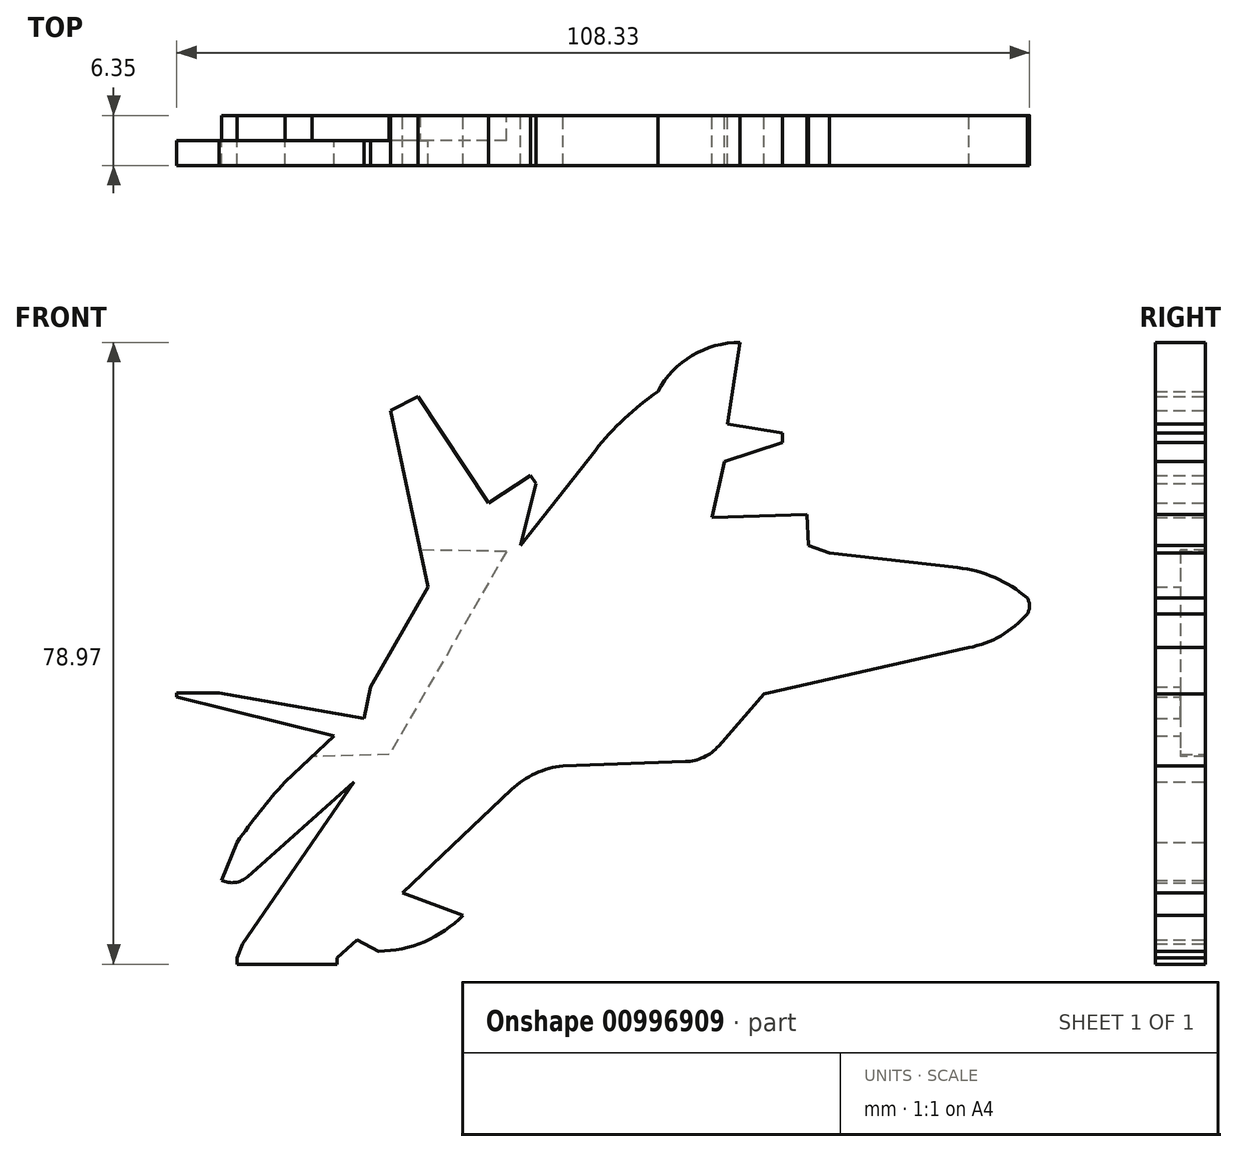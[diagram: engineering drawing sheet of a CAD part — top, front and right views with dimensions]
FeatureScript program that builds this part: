
annotation { "Feature Type Name" : "Feature", "Feature Type Description" : "" }
export const myFeature = defineFeature(function(context is Context, id is Id, definition is map)
    precondition{}
    {
        {
            var Q0;
            Q0=qCreatedBy(makeId("Front.planeOp"),FACE);
            var sketch = newSketch(context, id + "F0", { "sketchPlane" : qUnion([Q0])});
            skLineSegment(sketch, "E0", {"start": v(-31.83, -6.62) * mm, "end": v(-24.5, 6.08) * mm});
            skLineSegment(sketch, "E1", {"start": v(-24.5, 6.08) * mm, "end": v(-29.32, 28.52) * mm});
            skLineSegment(sketch, "E2", {"start": v(-29.32, 28.52) * mm, "end": v(-25.77, 30.29) * mm});
            skLineSegment(sketch, "E3", {"start": v(-25.77, 30.29) * mm, "end": v(-16.87, 16.76) * mm});
            skLineSegment(sketch, "E4", {"start": v(-16.87, 16.76) * mm, "end": v(-11.52, 20.28) * mm});
            skLineSegment(sketch, "E5", {"start": v(-11.52, 20.28) * mm, "end": v(-10.82, 19.22) * mm});
            skLineSegment(sketch, "E6", {"start": v(-10.82, 19.22) * mm, "end": v(-12.8, 11.37) * mm});
            skLineSegment(sketch, "E7", {"start": v(-12.8, 11.37) * mm, "end": v(-3.28, 23.46) * mm});
            skArc(sketch, "E8", {"start": v(4.67, 30.93) * mm, "mid": v(0.41, 27.5) * mm, "end": v(-3.28, 23.46) * mm});
            skArc(sketch, "E9", {"start": v(15.12, 37.16) * mm, "mid": v(9.03, 35.5) * mm, "end": v(4.67, 30.93) * mm});
            skLineSegment(sketch, "E10", {"start": v(15.12, 37.16) * mm, "end": v(13.48, 26.79) * mm});
            skLineSegment(sketch, "E11", {"start": v(13.48, 26.79) * mm, "end": v(20.5, 25.68) * mm});
            skLineSegment(sketch, "E12", {"start": v(20.5, 25.68) * mm, "end": v(20.5, 24.48) * mm});
            skLineSegment(sketch, "E13", {"start": v(20.5, 24.48) * mm, "end": v(13.12, 22.05) * mm});
            skLineSegment(sketch, "E14", {"start": v(13.12, 22.05) * mm, "end": v(11.53, 14.9) * mm});
            skLineSegment(sketch, "E15", {"start": v(11.53, 14.9) * mm, "end": v(23.64, 15.31) * mm});
            skLineSegment(sketch, "E16", {"start": v(23.64, 15.31) * mm, "end": v(23.77, 11.4) * mm});
            skLineSegment(sketch, "E17", {"start": v(23.77, 11.4) * mm, "end": v(26.46, 10.4) * mm});
            skLineSegment(sketch, "E18", {"start": v(26.46, 10.4) * mm, "end": v(42.75, 8.56) * mm});
            skArc(sketch, "E19", {"start": v(51.59, 4.7) * mm, "mid": v(47.46, 7.3) * mm, "end": v(42.75, 8.56) * mm});
            skArc(sketch, "E20", {"start": v(51.59, 2.7) * mm, "mid": v(51.88, 3.7) * mm, "end": v(51.59, 4.7) * mm});
            skArc(sketch, "E21", {"start": v(44.15, -1.6) * mm, "mid": v(48.24, -0.1) * mm, "end": v(51.59, 2.7) * mm});
            skLineSegment(sketch, "E22", {"start": v(44.15, -1.6) * mm, "end": v(18.14, -7.5) * mm});
            skLineSegment(sketch, "E23", {"start": v(18.14, -7.5) * mm, "end": v(12.4, -14.08) * mm});
            skArc(sketch, "E24", {"start": v(8.16, -16.1) * mm, "mid": v(10.49, -15.53) * mm, "end": v(12.4, -14.08) * mm});
            skLineSegment(sketch, "E25", {"start": v(8.16, -16.1) * mm, "end": v(-7.38, -16.6) * mm});
            skArc(sketch, "E26", {"start": v(-7.38, -16.6) * mm, "mid": v(-10.88, -17.59) * mm, "end": v(-13.9, -19.63) * mm});
            skLineSegment(sketch, "E27", {"start": v(-13.9, -19.63) * mm, "end": v(-27.78, -32.74) * mm});
            skLineSegment(sketch, "E28", {"start": v(-27.78, -32.74) * mm, "end": v(-20.07, -35.6) * mm});
            skArc(sketch, "E29", {"start": v(-30.81, -40.18) * mm, "mid": v(-24.99, -38.96) * mm, "end": v(-20.07, -35.6) * mm});
            skLineSegment(sketch, "E30", {"start": v(-30.81, -40.18) * mm, "end": v(-33.58, -38.72) * mm});
            skLineSegment(sketch, "E31", {"start": v(-33.58, -38.72) * mm, "end": v(-46.76, -50.69) * mm});
            skArc(sketch, "E32", {"start": v(-49.29, -51.48) * mm, "mid": v(-47.94, -51.36) * mm, "end": v(-46.76, -50.69) * mm});
            skLineSegment(sketch, "E33", {"start": v(-49.29, -51.48) * mm, "end": v(-52.27, -49.73) * mm});
            skLineSegment(sketch, "E34", {"start": v(-52.27, -49.73) * mm, "end": v(-48.1, -39.25) * mm});
            skLineSegment(sketch, "E35", {"start": v(-48.1, -39.25) * mm, "end": v(-33.9, -18.7) * mm});
            skLineSegment(sketch, "E36", {"start": v(-33.9, -18.7) * mm, "end": v(-47.44, -30.71) * mm});
            skArc(sketch, "E37", {"start": v(-50.76, -31.15) * mm, "mid": v(-49.03, -31.44) * mm, "end": v(-47.44, -30.71) * mm});
            skLineSegment(sketch, "E38", {"start": v(-50.76, -31.15) * mm, "end": v(-48.78, -26.37) * mm});
            skArc(sketch, "E39", {"start": v(-42.7, -18.7) * mm, "mid": v(-45.89, -22.42) * mm, "end": v(-48.78, -26.37) * mm});
            skLineSegment(sketch, "E40", {"start": v(-42.7, -18.7) * mm, "end": v(-36.44, -12.83) * mm});
            skLineSegment(sketch, "E41", {"start": v(-36.44, -12.83) * mm, "end": v(-56.45, -7.89) * mm});
            skLineSegment(sketch, "E42", {"start": v(-56.45, -7.89) * mm, "end": v(-56.45, -7.36) * mm});
            skLineSegment(sketch, "E43", {"start": v(-56.45, -7.36) * mm, "end": v(-51.06, -7.36) * mm});
            skLineSegment(sketch, "E44", {"start": v(-51.06, -7.36) * mm, "end": v(-32.68, -10.58) * mm});
            skLineSegment(sketch, "E45", {"start": v(-32.68, -10.58) * mm, "end": v(-31.83, -6.62) * mm});
            skLineSegment(sketch, "E46", {"start": v(-31.83, -6.62) * mm, "end": v(0, -6.62) * mm, "construction": true});
            skSolve(sketch);
        }
        {
            var Q0;
            Q0 = qSketchRegion(id + "F0", true);
            extrude(context, id + "F1", {"entities" : qUnion([Q0]), "depth" : 6.35 * mm, "offsetDistance" : 25.4 * mm});
        }
        {
            var Q0;
            Q0=makeQuery(id+"F1.opExtrude","CAP_FACE",FACE,{"disambiguationData":[OSD([sQuery(id+"F0.wireOp",EDGE,"E0"),sQuery(id+"F0.wireOp",EDGE,"E1"),sQuery(id+"F0.wireOp",EDGE,"E2"),sQuery(id+"F0.wireOp",EDGE,"E3"),sQuery(id+"F0.wireOp",EDGE,"E4"),sQuery(id+"F0.wireOp",EDGE,"E5"),sQuery(id+"F0.wireOp",EDGE,"E6"),sQuery(id+"F0.wireOp",EDGE,"E7"),sQuery(id+"F0.wireOp",EDGE,"E8"),sQuery(id+"F0.wireOp",EDGE,"E9"),sQuery(id+"F0.wireOp",EDGE,"E10"),sQuery(id+"F0.wireOp",EDGE,"E11"),sQuery(id+"F0.wireOp",EDGE,"E12"),sQuery(id+"F0.wireOp",EDGE,"E13"),sQuery(id+"F0.wireOp",EDGE,"E14"),sQuery(id+"F0.wireOp",EDGE,"E15"),sQuery(id+"F0.wireOp",EDGE,"E16"),sQuery(id+"F0.wireOp",EDGE,"E17"),sQuery(id+"F0.wireOp",EDGE,"E18"),sQuery(id+"F0.wireOp",EDGE,"E19"),sQuery(id+"F0.wireOp",EDGE,"E20"),sQuery(id+"F0.wireOp",EDGE,"E21"),sQuery(id+"F0.wireOp",EDGE,"E22"),sQuery(id+"F0.wireOp",EDGE,"E23"),sQuery(id+"F0.wireOp",EDGE,"E24"),sQuery(id+"F0.wireOp",EDGE,"E25"),sQuery(id+"F0.wireOp",EDGE,"E26"),sQuery(id+"F0.wireOp",EDGE,"E27"),sQuery(id+"F0.wireOp",EDGE,"E28"),sQuery(id+"F0.wireOp",EDGE,"E29"),sQuery(id+"F0.wireOp",EDGE,"E30"),sQuery(id+"F0.wireOp",EDGE,"E31"),sQuery(id+"F0.wireOp",EDGE,"E32"),sQuery(id+"F0.wireOp",EDGE,"E33"),sQuery(id+"F0.wireOp",EDGE,"E34"),sQuery(id+"F0.wireOp",EDGE,"E35"),sQuery(id+"F0.wireOp",EDGE,"E36"),sQuery(id+"F0.wireOp",EDGE,"E37"),sQuery(id+"F0.wireOp",EDGE,"E38"),sQuery(id+"F0.wireOp",EDGE,"E39"),sQuery(id+"F0.wireOp",EDGE,"E40"),sQuery(id+"F0.wireOp",EDGE,"E41"),sQuery(id+"F0.wireOp",EDGE,"E42"),sQuery(id+"F0.wireOp",EDGE,"E43"),sQuery(id+"F0.wireOp",EDGE,"E44"),sQuery(id+"F0.wireOp",EDGE,"E45")])],"isStart":false});
            var sketch = newSketch(context, id + "F2", { "sketchPlane" : qUnion([Q0])});
            skLineSegment(sketch, "E47", {"start": v(-36.1, -41.02) * mm, "end": v(-36.1, -51.5) * mm});
            skLineSegment(sketch, "E48", {"start": v(-36.1, -51.5) * mm, "end": v(-61.5, -51.5) * mm});
            skLineSegment(sketch, "E49", {"start": v(-61.5, -41.02) * mm, "end": v(-61.5, -51.5) * mm});
            skLineSegment(sketch, "E50", {"start": v(-36.1, -41.02) * mm, "end": v(-48.8, -41.02) * mm});
            skLineSegment(sketch, "E51", {"start": v(-48.8, -41.02) * mm, "end": v(-61.5, -41.02) * mm});
            skSolve(sketch);
        }
        {
            var Q0;
            Q0 = qSketchRegion(id + "F2", true);
            extrude(context, id + "F3", {"entities" : qUnion([Q0]), "operationType" : NewBodyOperationType.REMOVE, "endBound" : BoundingType.THROUGH_ALL, "oppositeDirection" : true, "depth" : 25.4 * mm, "offsetDistance" : 25.4 * mm});
        }
        {
            var Q0;
            Q0=makeQuery(id+"F1.opExtrude","CAP_FACE",FACE,{"disambiguationData":[OSD([sQuery(id+"F0.wireOp",EDGE,"E0"),sQuery(id+"F0.wireOp",EDGE,"E1"),sQuery(id+"F0.wireOp",EDGE,"E2"),sQuery(id+"F0.wireOp",EDGE,"E3"),sQuery(id+"F0.wireOp",EDGE,"E4"),sQuery(id+"F0.wireOp",EDGE,"E5"),sQuery(id+"F0.wireOp",EDGE,"E6"),sQuery(id+"F0.wireOp",EDGE,"E7"),sQuery(id+"F0.wireOp",EDGE,"E8"),sQuery(id+"F0.wireOp",EDGE,"E9"),sQuery(id+"F0.wireOp",EDGE,"E10"),sQuery(id+"F0.wireOp",EDGE,"E11"),sQuery(id+"F0.wireOp",EDGE,"E12"),sQuery(id+"F0.wireOp",EDGE,"E13"),sQuery(id+"F0.wireOp",EDGE,"E14"),sQuery(id+"F0.wireOp",EDGE,"E15"),sQuery(id+"F0.wireOp",EDGE,"E16"),sQuery(id+"F0.wireOp",EDGE,"E17"),sQuery(id+"F0.wireOp",EDGE,"E18"),sQuery(id+"F0.wireOp",EDGE,"E19"),sQuery(id+"F0.wireOp",EDGE,"E20"),sQuery(id+"F0.wireOp",EDGE,"E21"),sQuery(id+"F0.wireOp",EDGE,"E22"),sQuery(id+"F0.wireOp",EDGE,"E23"),sQuery(id+"F0.wireOp",EDGE,"E24"),sQuery(id+"F0.wireOp",EDGE,"E25"),sQuery(id+"F0.wireOp",EDGE,"E26"),sQuery(id+"F0.wireOp",EDGE,"E27"),sQuery(id+"F0.wireOp",EDGE,"E28"),sQuery(id+"F0.wireOp",EDGE,"E29"),sQuery(id+"F0.wireOp",EDGE,"E30"),sQuery(id+"F0.wireOp",EDGE,"E31"),sQuery(id+"F0.wireOp",EDGE,"E32"),sQuery(id+"F0.wireOp",EDGE,"E33"),sQuery(id+"F0.wireOp",EDGE,"E34"),sQuery(id+"F0.wireOp",EDGE,"E35"),sQuery(id+"F0.wireOp",EDGE,"E36"),sQuery(id+"F0.wireOp",EDGE,"E37"),sQuery(id+"F0.wireOp",EDGE,"E38"),sQuery(id+"F0.wireOp",EDGE,"E39"),sQuery(id+"F0.wireOp",EDGE,"E40"),sQuery(id+"F0.wireOp",EDGE,"E41"),sQuery(id+"F0.wireOp",EDGE,"E42"),sQuery(id+"F0.wireOp",EDGE,"E43"),sQuery(id+"F0.wireOp",EDGE,"E44"),sQuery(id+"F0.wireOp",EDGE,"E45")])],"isStart":true});
            var sketch = newSketch(context, id + "F4", { "sketchPlane" : qUnion([Q0])});
            skLineSegment(sketch, "E52", {"start": v(14.56, 10.6) * mm, "end": v(29.45, -15.19) * mm});
            skLineSegment(sketch, "E53", {"start": v(56.45, -15.9) * mm, "end": v(56.45, 11.32) * mm});
            skLineSegment(sketch, "E54", {"start": v(32.68, -10.58) * mm, "end": v(32.68, -15.27) * mm, "construction": true});
            skLineSegment(sketch, "E55", {"start": v(24.5, 6.08) * mm, "end": v(24.5, 10.78) * mm, "construction": true});
            skLineSegment(sketch, "E56", {"start": v(14.56, 10.6) * mm, "end": v(56.45, 11.32) * mm});
            skLineSegment(sketch, "E57", {"start": v(29.45, -15.19) * mm, "end": v(56.45, -15.9) * mm});
            skLineSegment(sketch, "E58", {"start": v(29.45, -15.19) * mm, "end": v(99.07, -15.19) * mm, "construction": true});
            skLineSegment(sketch, "E59", {"start": v(14.56, 10.6) * mm, "end": v(99.07, 10.6) * mm, "construction": true});
            skLineSegment(sketch, "E60", {"start": v(56.45, 11.32) * mm, "end": v(99.07, 10.6) * mm, "construction": true});
            skLineSegment(sketch, "E61", {"start": v(99.07, -15.19) * mm, "end": v(56.45, -15.9) * mm, "construction": true});
            skSolve(sketch);
        }
        {
            var Q0;
            Q0 = qSketchRegion(id + "F4", true);
            extrude(context, id + "F5", {"entities" : qUnion([Q0]), "operationType" : NewBodyOperationType.REMOVE, "oppositeDirection" : true, "depth" : 3.17 * mm, "offsetDistance" : 25.4 * mm});
        }
        {
            var Q0;
            Q0=makeQuery(id+"F3.boolean.opBoolean","COPY",FACE,{"derivedFrom":makeQuery(id+"F3.opExtrude","SWEPT_FACE",FACE,{"disambiguationData":[OSD([sQuery(id+"F2.wireOp",EDGE,"E50"),sQuery(id+"F2.wireOp",EDGE,"E51")])]})});
            var sketch = newSketch(context, id + "F6", { "sketchPlane" : qUnion([Q0])});
            skLineSegment(sketch, "E62.bottom", {"start": v(-48.8, 6.35) * mm, "end": v(-36.1, 6.35) * mm});
            skLineSegment(sketch, "E62.top", {"start": v(-48.8, 0) * mm, "end": v(-36.1, 0) * mm});
            skLineSegment(sketch, "E62.left", {"start": v(-48.8, 6.35) * mm, "end": v(-48.8, 0) * mm});
            skLineSegment(sketch, "E62.right", {"start": v(-36.1, 6.35) * mm, "end": v(-36.1, 0) * mm});
            skSolve(sketch);
        }
        {
            var Q0;
            Q0 = qSketchRegion(id + "F6", true);
            extrude(context, id + "F7", {"entities" : qUnion([Q0]), "operationType" : NewBodyOperationType.ADD, "depth" : 0.8 * mm, "offsetDistance" : 25.4 * mm});
        }
    });
